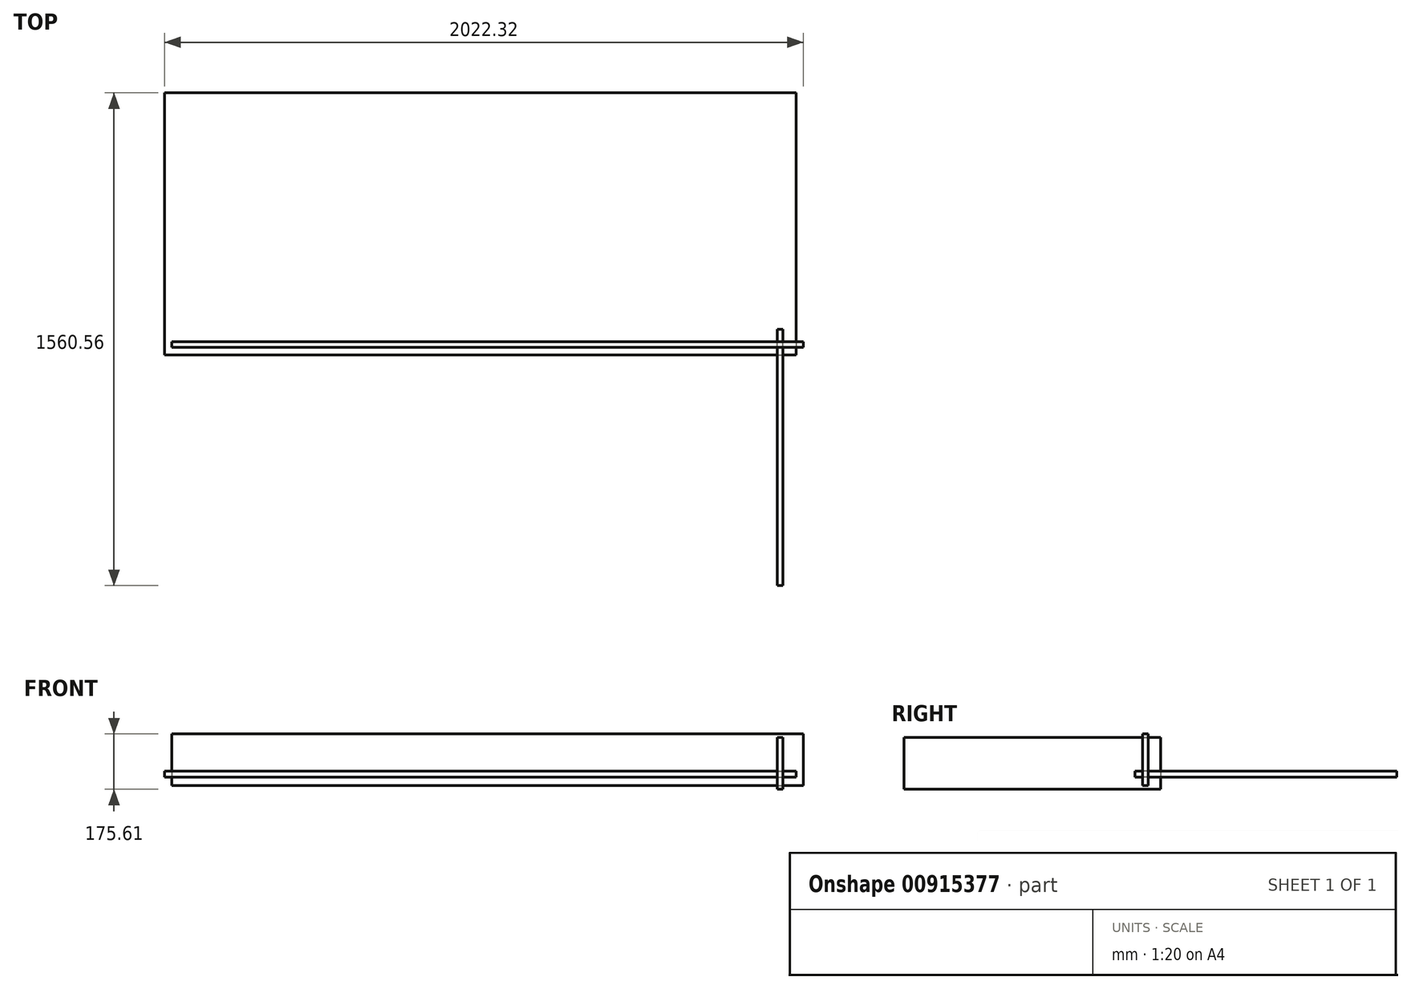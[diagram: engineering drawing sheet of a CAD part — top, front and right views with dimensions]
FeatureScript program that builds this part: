
annotation { "Feature Type Name" : "Feature", "Feature Type Description" : "" }
export const myFeature = defineFeature(function(context is Context, id is Id, definition is map)
    precondition{}
    {
        {
            var Q0;
            Q0=qCreatedBy(makeId("Top.planeOp"),FACE);
            var sketch = newSketch(context, id + "F0", { "sketchPlane" : qUnion([Q0])});
            skLineSegment(sketch, "E0.bottom", {"start": v(-1940.03, 787.81) * mm, "end": v(59.97, 787.81) * mm});
            skLineSegment(sketch, "E0.top", {"start": v(-1940.03, -42.19) * mm, "end": v(59.97, -42.19) * mm});
            skLineSegment(sketch, "E0.left", {"start": v(-1940.03, 787.81) * mm, "end": v(-1940.03, -42.19) * mm});
            skLineSegment(sketch, "E0.right", {"start": v(59.97, 787.81) * mm, "end": v(59.97, -42.19) * mm});
            skSolve(sketch);
        }
        {
            var Q0;
            Q0 = qSketchRegion(id + "F0", true);
            extrude(context, id + "F1", {"entities" : qUnion([Q0]), "depth" : 18 * mm, "offsetDistance" : 25 * mm});
        }
        {
            var Q0;
            Q0=qCreatedBy(makeId("Front.planeOp"),FACE);
            var sketch = newSketch(context, id + "F2", { "sketchPlane" : qUnion([Q0])});
            skLineSegment(sketch, "E1.bottom", {"start": v(-1917.71, 136.51) * mm, "end": v(82.29, 136.51) * mm});
            skLineSegment(sketch, "E1.top", {"start": v(-1917.71, -27.49) * mm, "end": v(82.29, -27.49) * mm});
            skLineSegment(sketch, "E1.left", {"start": v(-1917.71, 136.51) * mm, "end": v(-1917.71, -27.49) * mm});
            skLineSegment(sketch, "E1.right", {"start": v(82.29, 136.51) * mm, "end": v(82.29, -27.49) * mm});
            skSolve(sketch);
        }
        {
            var Q0;
            Q0 = qSketchRegion(id + "F2", true);
            extrude(context, id + "F3", {"entities" : qUnion([Q0]), "depth" : 18 * mm, "offsetDistance" : 25 * mm});
        }
        {
            var Q0;
            Q0=qCreatedBy(makeId("Right.planeOp"),FACE);
            var sketch = newSketch(context, id + "F4", { "sketchPlane" : qUnion([Q0])});
            skLineSegment(sketch, "E2.bottom", {"start": v(-772.75, 124.9) * mm, "end": v(39.25, 124.9) * mm});
            skLineSegment(sketch, "E2.top", {"start": v(-772.75, -39.1) * mm, "end": v(39.25, -39.1) * mm});
            skLineSegment(sketch, "E2.left", {"start": v(-772.75, 124.9) * mm, "end": v(-772.75, -39.1) * mm});
            skLineSegment(sketch, "E2.right", {"start": v(39.25, 124.9) * mm, "end": v(39.25, -39.1) * mm});
            skSolve(sketch);
        }
        {
            var Q0;
            Q0 = qSketchRegion(id + "F4", true);
            extrude(context, id + "F5", {"entities" : qUnion([Q0]), "depth" : 18 * mm, "offsetDistance" : 25 * mm});
        }
    });
